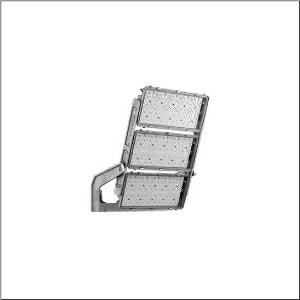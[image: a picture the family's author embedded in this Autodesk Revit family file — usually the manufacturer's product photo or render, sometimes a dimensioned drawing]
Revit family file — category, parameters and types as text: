
# Revit family: floodlight_fl_11_maxi_pro_remote___pl33t_5xa779427f01ba_72f0
name_source: partatom
category: Lighting Fixtures
units: mm (PartAtom-declared; Revit-internal decimal feet)

## family parameters
Cut with Voids When Loaded = No
Host = Face
Light Source = No
Part Type = Normal
Room Calculation Point = No
Round Connector Dimension = Use Diameter
Shared = No

## types (1)
- --- (1 x LED, 132850 lm, 953.7 W, 5000K)
    Apparent Load = 954 VA
    CIE Flux Codes = 25 74 99 100 100
    Color Rendering = 70
    Color Temperature = 5000K
    Default Elevation = 1800 mm
    Description = Floodlight FL 11  maxi  pro Remote floodlight; light control with lens of PMMA; cover panel of toughened safety glass, transparent; light distribution: PL33T, asymmetric direct distribution, LEDcolour temperature: 5000K, colour rendering: CRI > 70, light colour: 750; brightness control: DALI 2 (1 DALI address); with terminal, 8-pole, max. 2.5mm², mains connection: 220..240V/380..400V AC, 50/60Hz, surge voltage resistance: line to ground: 10kV, ECG replaceable separately, no afterglow with DALI off / DMX off command, LED unit replaceable without ESD environment, dustproof LED module, dimming range 10..100%; floodlight with 2x LED unit of diecast aluminium, coated grey; length: 713mm / width: 651mm / height: 338mm; mounting bracket, of diecast aluminium, uncoated, natural, equipment: Power, protection rating (complete): IP66; insulation class (complete): insulation class I (protective earthing); certification: CE, ENEC, VDE; ball protection: ball impact resistance with accessories, only for outdoor installations, rated ambient temperature 10°C, permissible operating ambient temperature: -40..+30°C, permissible storage temperature: -40..+85°C; packaging unit: 1 piece

Light Distribution: PL33T
    Height = 320 mm
    Lamp = 1 x LED
    Lamp Light Flux = 132850 lm
    Lamp Power = 953.7 W
    Lamp count = 1
    Length = 1002 mm
    Luminous efficacy = 139 lm/W
    Manufacturer = Siteco
    ModVariant = No
    Model = 5XA779427F01BA
    Number of Poles = 1
    OnlyDefault = Yes
    Power Factor = 1
    Product Name = Floodlight FL 11 maxi pro Remote | PL33T
    Product group = floodlight | pylon top
    ProductGroupID = 6101
    Protection Class = Protection class I
    Protection Degree = IP 66
    RLX_Detail_Level = 1
    RlxData = <blob elided: 52209 chars, md5=73e16f04>
    Socket = socket
    Standby Power = 0 W
    System Light Flux = 132850 lm
    System Power = 954 W
    Type Comments = factory setting: luminous flux: 100 % | dim-lin: 254 | 665 mA
    Type Image = l_1006784.jpg
    URL = http://relux.com
    VarID = @adj_006539
    Voltage = 0 V
    Weight = 0.00 kg
    Width = 655 mm

## geometry (parser evidence)
native form markers: Blend x4, Sweep x12
no freeform markers — native parametric forms only
